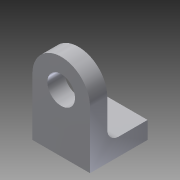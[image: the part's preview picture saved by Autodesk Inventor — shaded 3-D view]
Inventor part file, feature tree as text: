
AUTODESK INVENTOR PART (.ipt)
format: ipt  version: 2015 (Build 190159000, 159)  size: 101,376 bytes
history: native  units: mm
features: extrude x2, sketch x2, other x1, fillet x1
ambient origin geometry x8: Origin, YZ Plane, XZ Plane, XY Plane, X Axis, Y Axis, Z Axis, Center Point
bodies: Body1 (feature_tree)
feature tree (6):
  other  "Sólido1"
  extrude  "Extrusión1"  Depth=5.0mm
  extrude  "Extrusión2"  Depth=1.5mm TaperAngle=0.0deg
  fillet  "Empalme1"  Radius=5.0mm
  sketch  "Boceto2"  dims[d2=5.0mm d3=5.0mm]
  sketch  "Boceto3"  dims[d4=2.4mm d5=1.5mm d6=0.0mm d7=5.0mm d8=1.5mm d9=5.0mm d10=0.0mm d11=1.0mm]
